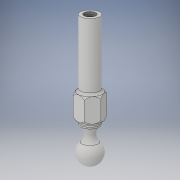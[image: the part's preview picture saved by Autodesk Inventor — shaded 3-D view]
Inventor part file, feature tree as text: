
AUTODESK INVENTOR PART (.ipt)
format: ipt  version: 2018 (Build 220112000, 112)  size: 201,728 bytes
history: native  units: mm
features: sketch x4, extrude x3, revolve x1, thread x1, plane x1, fillet x1
ambient origin geometry x8: Origin, YZ Plane, XZ Plane, XY Plane, X Axis, Y Axis, Z Axis, Center Point
bodies: Solid1 (feature_tree)
feature tree (11):
  revolve  "Revolution1"  [1 undecoded]
  thread  "Thread1"  [1 undecoded]
  plane  "Work Plane1"
  extrude  "Extrusion1"  Depth=0.5mm
  extrude  "Extrusion2"  Depth=0.75mm
  extrude  "Extrusion3"  Depth=0.5mm
  fillet  "Fillet1"  [1 undecoded]
  sketch  "Sketch1"  dims[d0=5.0mm d2=3.3mm d3=4.0mm]
  sketch  "Sketch2"  dims[d4=25.0mm d6=0.5mm]
  sketch  "Sketch3"  dims[d8=20.0mm d9=0.75mm]
  sketch  "Sketch4"  dims[d10=19.74597mm d11=5.0mm d12=90.0deg d13=10.0mm d14=0.0mm d15=-14.0mm d16=5.0mm d17=5.0mm d18=0.0mm d19=40.0mm d20=40.0mm d21=6.108652mm d22=0.0mm d23=40.0mm d24=40.0mm d25=6.108652mm d26=0.0mm d27=0.5mm]
note: 3 required parameter values undecoded (feature->parameter linkage not recoverable at this tier; creation-order binding heuristic only, values carry confidence <= 0.55)